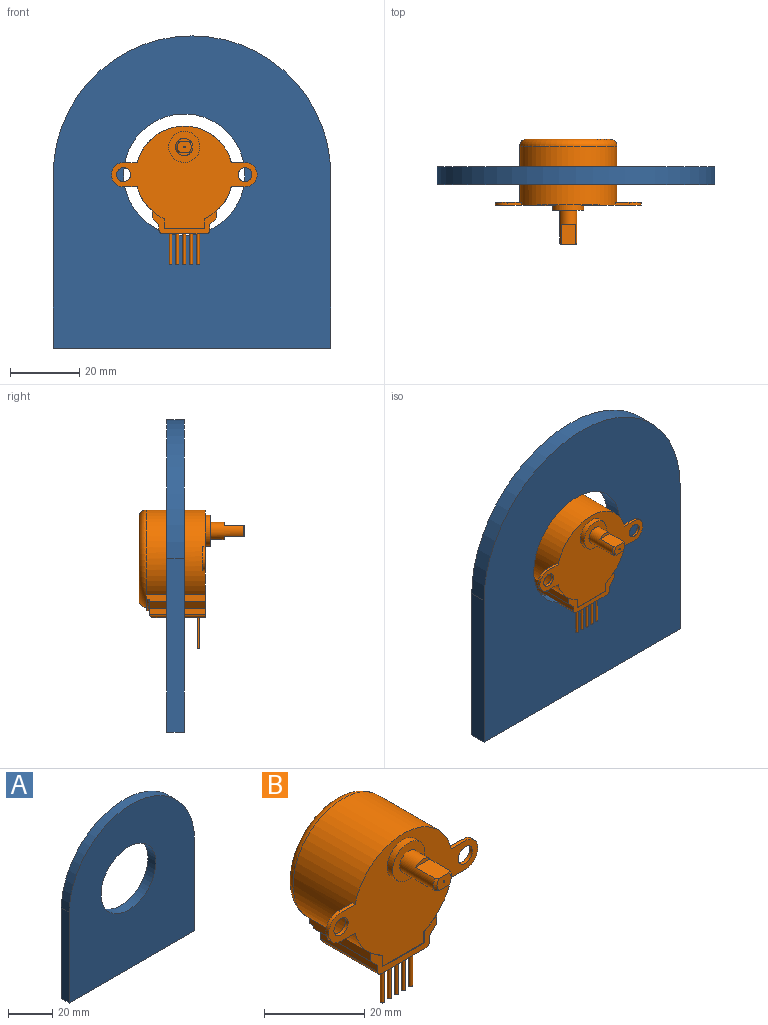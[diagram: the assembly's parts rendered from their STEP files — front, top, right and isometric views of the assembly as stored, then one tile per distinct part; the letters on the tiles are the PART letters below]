
ASSEMBLY  parts=2 mates=1
PART A: 7 faces, bbox 80x5x90 mm
  f0: plane 50x5mm, normal (1,0,0), area 250mm2, adj f1,f4,f5,f6
  f1: cylinder r=40mm len=80mm, axis (0,1,0), area 628.3mm2, adj f0,f2,f5,f6
  f2: plane 50x5mm, normal (-1,0,0), area 250mm2, adj f1,f4,f5,f6
  f3: cylinder r=17.5mm len=35mm, axis (0,1,0), area 549.8mm2, adj f5,f6
  f4: plane 80x5mm, normal (0,0,-1), area 400mm2, adj f0,f2,f5,f6
  f5: plane 90x80mm, normal (0,-1,0), area 5551.2mm2, adj f0,f1,f2,f3,f4
  f6: plane 90x80mm, normal (0,1,0), area 5551.2mm2, adj f0,f1,f2,f3,f4
PART B: 152 faces, bbox 42.1x30.6x41.2 mm
  f0: cone r=500mm half-angle=30deg, axis (0,-1,0), area 0.3mm2, adj f139
  f1: cone r=2.5mm half-angle=45deg, axis (0,1,0), area 2.4mm2, adj f9,f12,f138,f139
  f2: plane 0.8x0.8mm, normal (0,0,-1), area 0.5mm2, adj f66
  f3: plane 24x24mm, normal (0,1,0), area 396.9mm2, adj f15,f16,f21,f22,f23,f24,f25,f26
  f4: cylinder r=14mm len=28mm, axis (0,1,0), area 1138.2mm2, adj f13,f67,f72,f73,f74,f75,f76,f77
  f5: plane 0.88x0.76mm, normal (0,1,0), area 0.5mm2, adj f89
  f6: plane 0.76x0.55mm, normal (0,1,0), area 0.4mm2, adj f107,f109
  f7: plane 0.88x0.59mm, normal (0,1,0), area 0.5mm2, adj f106,f108
  f8: plane 2.91x2.69mm, normal (0,1,0), area 6.3mm2, adj f104,f105,f106,f107,f108,f109,f110
  f9: plane 6.08x4.08mm, normal (0,0,-1), area 23.7mm2, adj f1,f10,f65,f138,f139
  f10: plane 4x1mm, normal (0,-1,0), area 2.8mm2, adj f9,f138
  f11: plane 4x1mm, normal (0,-1,0), area 2.8mm2, adj f12,f138
  f12: plane 6.08x4.08mm, normal (0,0,1), area 23.7mm2, adj f1,f11,f65,f138,f139
  f13: plane 17.16x2.07mm, normal (-1,0,0), area 33.6mm2, adj f4,f14,f54,f56,f60,f61,f62,f64
  f14: torus R=14.8mm, axis (0,1,0), area 6.3mm2, adj f13,f60,f61,f147
  f15: extruded ~2.28x0.58mm, area 0.3mm2, adj f3,f16,f93,f141
  f16: plane 0.86x0.12mm, normal (-0.14,0,-0.99), area 0.1mm2, adj f3,f15,f94,f141
  f17: plane 2.95x2.54mm, normal (0,1,0), area 4.2mm2, adj f18,f19,f20,f21,f22,f23,f24,f25
  f18: plane 0.93x0.78mm, normal (0.76,0,0.65), area 0.1mm2, adj f17,f19,f20,f92
  f19: plane 0.78x0.1mm, normal (0,0,-1), area 0.1mm2, adj f17,f18,f20,f92
  f20: plane 0.93x0.1mm, normal (-1,0,0), area 0.1mm2, adj f17,f18,f19,f92
  f21: plane 0.54x0.1mm, normal (1,0,0), area 0.1mm2, adj f3,f17,f22,f31
  f22: plane 0.36x0.1mm, normal (0,0,1), area 0mm2, adj f3,f17,f21,f23
  f23: plane 0.63x0.1mm, normal (1,0,0), area 0.1mm2, adj f3,f17,f22,f24
  f24: plane 0.36x0.1mm, normal (0,0,-1), area 0mm2, adj f3,f17,f23,f25
  f25: plane 1.79x0.1mm, normal (1,0,0), area 0.2mm2, adj f3,f17,f24,f26
  f26: plane 0.7x0.1mm, normal (0,0,-1), area 0.1mm2, adj f3,f17,f25,f27
  f27: plane 1.75x1.47mm, normal (-0.76,0,-0.64), area 0.2mm2, adj f3,f17,f26,f28
  f28: plane 0.67x0.1mm, normal (-1,0,0), area 0.1mm2, adj f3,f17,f27,f29
  f29: plane 1.47x0.1mm, normal (0,0,1), area 0.1mm2, adj f3,f17,f28,f30
  f30: plane 0.54x0.1mm, normal (-1,0,0), area 0.1mm2, adj f3,f17,f29,f31
  f31: plane 0.7x0.1mm, normal (0,0,1), area 0.1mm2, adj f3,f17,f21,f30
  f32: plane 3x2.38mm, normal (0,1,0), area 5mm2, adj f33,f88,f89,f90
  f33: extruded ~0.67x0.66mm, area 0.2mm2, adj f32,f91
  f34: extruded ~2.42x2mm, area 0.6mm2, adj f3,f35,f86,f140
  f35: plane 0.43x0.1mm, normal (0.99,0,0.15), area 0mm2, adj f3,f34,f36,f140
  f36: plane 1.31x0.1mm, normal (0,0,1), area 0.1mm2, adj f3,f35,f37,f140
  f37: plane 0.64x0.1mm, normal (1,0,0), area 0.1mm2, adj f3,f36,f38,f140
  f38: plane 1.93x0.1mm, normal (0,0,-1), area 0.2mm2, adj f3,f37,f39,f140
  f39: plane 1.56x0.25mm, normal (-0.99,0,-0.16), area 0.2mm2, adj f3,f38,f40,f140
  f40: plane 0.69x0.1mm, normal (-0.14,0,0.99), area 0.1mm2, adj f3,f39,f87,f140
  f41: plane 3.15x2.91mm, normal (0,1,0), area 4.6mm2, adj f42,f43,f44,f45,f46,f47,f48
  f42: plane 2.91x1.08mm, normal (0.94,0,0.35), area 0.3mm2, adj f3,f41,f43,f48
  f43: plane 0.91x0.1mm, normal (0,0,-1), area 0.1mm2, adj f3,f41,f42,f44
  f44: plane 2.09x0.65mm, normal (-0.96,0,-0.3), area 0.2mm2, adj f3,f41,f43,f45
  f45: plane 2.09x0.65mm, normal (0.95,0,-0.3), area 0.2mm2, adj f3,f41,f44,f46
  f46: plane 0.94x0.1mm, normal (0,0,-1), area 0.1mm2, adj f3,f41,f45,f47
  f47: plane 2.91x1.1mm, normal (-0.94,0,0.35), area 0.3mm2, adj f3,f41,f46,f48
  f48: plane 0.97x0.1mm, normal (0,0,1), area 0.1mm2, adj f3,f41,f42,f47
  f49: plane 2.91x2.67mm, normal (0,1,0), area 5.8mm2, adj f50,f51,f83,f84
  f50: plane 1.59x0.1mm, normal (1,0,0), area 0.2mm2, adj f49,f51,f85
  f51: extruded ~1.59x0.87mm, area 0.3mm2, adj f49,f50,f85
  f52: extruded ~1.66x1.15mm, area 0.4mm2, adj f3,f53,f81,f151
  f53: plane 0.79x0.18mm, normal (0.22,0,0.98), area 0.1mm2, adj f3,f52,f82,f151
  f54: plane 18.6x6.54mm, normal (0,-1,0), area 39.8mm2, adj f13,f55,f56,f57,f58,f59,f63,f64
  f55: plane 2.76x0.1mm, normal (1,0,0), area 0.3mm2, adj f54,f56,f59,f67
  f56: cylinder r=14mm len=3.5mm, axis (0,-1,0), area 0.4mm2, adj f13,f54,f55,f67
  f57: cylinder r=14mm len=3.5mm, axis (0,-1,0), area 0.4mm2, adj f54,f58,f67,f147
  f58: plane 2.76x0.1mm, normal (-1,0,0), area 0.3mm2, adj f54,f57,f59,f67
  f59: plane 11.6x0.1mm, normal (0,0,1), area 1.2mm2, adj f54,f55,f58,f67
  f60: plane 18.6x4.34mm, normal (0,1,0), area 16.2mm2, adj f13,f14,f80,f147
  f61: cylinder r=15mm len=18.6mm, axis (0,1,0), area 12mm2, adj f13,f14,f145,f147
  f62: plane 18.6x3.98mm, normal (0,1,0), area 23.6mm2, adj f13,f63,f64,f145,f147,f148,f149,f150
  f63: plane 16.1x1.53mm, normal (-1,0,0), area 24.6mm2, adj f54,f62,f64,f144
  f64: plane 16.1x2mm, normal (-0.71,0,-0.71), area 45.6mm2, adj f13,f54,f62,f63
  f65: cone r=2.5mm half-angle=45deg, axis (0,1,0), area 2.4mm2, adj f9,f12,f138,f139
  f66: cylinder r=0.4mm len=10mm, axis (0,0,-1), area 25.1mm2, adj f2,f137
  f67: plane 42x29.5mm, normal (0,-1,0), area 638.7mm2, adj f4,f55,f56,f57,f58,f59,f68,f70
  f68: cylinder r=4.5mm len=9mm, axis (0,-1,0), area 42.4mm2, adj f67,f69
  f69: plane 9x9mm, normal (0,-1,0), area 44mm2, adj f68,f138
  f70: cylinder r=3.5mm len=7mm, axis (0,1,0), area 8.8mm2, adj f67,f72,f73,f74
  f71: cylinder r=2mm len=4mm, axis (0,1,0), area 10.1mm2, adj f67,f72
  f72: plane 7.44x7mm, normal (0,1,0), area 32.2mm2, adj f4,f70,f71,f73,f74
  f73: plane 3.94x0.8mm, normal (0,0,1), area 3.2mm2, adj f4,f67,f70,f72
  f74: plane 3.94x0.8mm, normal (0,0,-1), area 3.2mm2, adj f4,f67,f70,f72
  f75: plane 7.44x7mm, normal (0,1,0), area 32.2mm2, adj f4,f76,f77,f78,f79
  f76: plane 3.94x0.8mm, normal (0,0,-1), area 3.2mm2, adj f4,f67,f75,f78
  f77: plane 3.94x0.8mm, normal (0,0,1), area 3.2mm2, adj f4,f67,f75,f78
  f78: cylinder r=3.5mm len=7mm, axis (0,1,0), area 8.8mm2, adj f67,f75,f76,f77
  f79: cylinder r=2mm len=4mm, axis (0,1,0), area 10.1mm2, adj f67,f75
  f80: torus R=12mm, axis (0,1,0), area 262mm2, adj f3,f4,f60
  f81: plane 0.78x0.24mm, normal (0.29,0,-0.96), area 0.1mm2, adj f3,f52,f82,f151
  f82: extruded ~3x2.83mm, area 0.8mm2, adj f3,f53,f81,f151
  f83: extruded ~2.91x2.67mm, area 0.7mm2, adj f3,f49,f84
  f84: plane 2.91x0.1mm, normal (-1,0,0), area 0.3mm2, adj f3,f49,f83
  f85: plane 1.59x0.87mm, normal (0,1,0), area 1.3mm2, adj f50,f51
  f86: plane 0.82x0.1mm, normal (-0.11,0,-0.99), area 0.1mm2, adj f3,f34,f87,f140
  f87: extruded ~1.02x0.82mm, area 0.3mm2, adj f3,f40,f86,f140
  f88: extruded ~2.19x1.39mm, area 0.5mm2, adj f3,f32,f90
  f89: extruded ~0.87x0.76mm, area 0.3mm2, adj f5,f32
  f90: extruded ~2.38x1.61mm, area 0.5mm2, adj f3,f32,f88
  f91: plane 0.67x0.66mm, normal (0,1,0), area 0.4mm2, adj f33
  f92: plane 0.93x0.78mm, normal (0,1,0), area 0.4mm2, adj f18,f19,f20
  f93: plane 0.9x0.1mm, normal (0,0,-1), area 0.1mm2, adj f3,f15,f94,f141
  f94: extruded ~2.95x2.34mm, area 0.5mm2, adj f3,f16,f93,f141
  f95: plane 1.22x0.1mm, normal (-1,0,0), area 0.1mm2, adj f3,f96,f103,f142
  f96: plane 1.69x1.13mm, normal (-0.83,0,0.56), area 0.2mm2, adj f3,f95,f97,f142
  f97: plane 1x0.1mm, normal (0,0,-1), area 0.1mm2, adj f3,f96,f98,f142
  f98: plane 0.97x0.59mm, normal (0.86,0,-0.52), area 0.1mm2, adj f3,f97,f99,f142
  f99: plane 0.97x0.59mm, normal (-0.86,0,-0.52), area 0.1mm2, adj f3,f98,f100,f142
  f100: plane 0.99x0.1mm, normal (0,0,-1), area 0.1mm2, adj f3,f99,f101,f142
  f101: plane 1.69x1.13mm, normal (0.83,0,0.56), area 0.2mm2, adj f3,f100,f102,f142
  f102: plane 1.22x0.1mm, normal (1,0,0), area 0.1mm2, adj f3,f101,f103,f142
  f103: plane 0.9x0.1mm, normal (0,0,1), area 0.1mm2, adj f3,f95,f102,f142
  f104: extruded ~2.69x1.55mm, area 0.4mm2, adj f3,f8,f105,f110
  f105: plane 2.91x0.1mm, normal (-1,0,0), area 0.3mm2, adj f3,f8,f104,f110
  f106: plane 0.59x0.1mm, normal (1,0,0), area 0.1mm2, adj f7,f8,f108
  f107: plane 0.55x0.1mm, normal (1,0,0), area 0.1mm2, adj f6,f8,f109
  f108: extruded ~0.88x0.59mm, area 0.2mm2, adj f7,f8,f106
  f109: extruded ~0.76x0.55mm, area 0.2mm2, adj f6,f8,f107
  f110: extruded ~2.55x1.36mm, area 0.4mm2, adj f3,f8,f104,f105
  f111: extruded ~2.19x1.39mm, area 0.5mm2, adj f3,f114,f143
  f112: extruded ~0.87x0.76mm, area 0.3mm2, adj f116,f143
  f113: extruded ~0.67x0.66mm, area 0.2mm2, adj f115,f143
  f114: extruded ~2.38x1.61mm, area 0.5mm2, adj f3,f111,f143
  f115: plane 0.67x0.66mm, normal (0,1,0), area 0.4mm2, adj f113
  f116: plane 0.88x0.76mm, normal (0,1,0), area 0.5mm2, adj f112
  f117: plane 1.26x0.1mm, normal (0,0,-1), area 0.1mm2, adj f3,f118,f122,f123
  f118: plane 0.66x0.1mm, normal (1,0,0), area 0.1mm2, adj f3,f117,f119,f123
  f119: plane 2.42x0.1mm, normal (0,0,1), area 0.2mm2, adj f3,f118,f120,f123
  f120: extruded ~2.4x1.6mm, area 0.4mm2, adj f3,f119,f121,f123
  f121: plane 0.81x0.1mm, normal (-0.08,0,1), area 0.1mm2, adj f3,f120,f122,f123
  f122: extruded ~2.34x2.3mm, area 0.5mm2, adj f3,f117,f121,f123
  f123: plane 2.95x2.42mm, normal (0,1,0), area 4.5mm2, adj f117,f118,f119,f120,f121,f122
  f124: plane 15.1x12.6mm, normal (0,0,-1), area 181.5mm2, adj f54,f125,f126,f127,f128,f144,f146,f148
  f125: plane 8x1mm, normal (0,1,0), area 8mm2, adj f124,f126,f128,f137
  f126: cylinder r=0.5mm len=1mm, axis (0,0,-1), area 1.6mm2, adj f124,f125,f127,f137
  f127: plane 8x1mm, normal (0,-1,0), area 8mm2, adj f124,f126,f128,f137
  f128: cylinder r=0.5mm len=1mm, axis (0,0,-1), area 1.6mm2, adj f124,f125,f127,f137
  f129: cylinder r=0.4mm len=10mm, axis (0,0,-1), area 25.1mm2, adj f130,f137
  f130: plane 0.8x0.8mm, normal (0,0,-1), area 0.5mm2, adj f129
  f131: cylinder r=0.4mm len=10mm, axis (0,0,-1), area 25.1mm2, adj f132,f137
  f132: plane 0.8x0.8mm, normal (0,0,-1), area 0.5mm2, adj f131
  f133: cylinder r=0.4mm len=10mm, axis (0,0,-1), area 25.1mm2, adj f134,f137
  f134: plane 0.8x0.8mm, normal (0,0,-1), area 0.5mm2, adj f133
  f135: cylinder r=0.4mm len=10mm, axis (0,0,-1), area 25.1mm2, adj f136,f137
  f136: plane 0.8x0.8mm, normal (0,0,-1), area 0.5mm2, adj f135
  f137: plane 9x1mm, normal (0,0,-1), area 6.3mm2, adj f66,f125,f126,f127,f128,f129,f131,f133
  f138: cylinder r=2.5mm len=9.5mm, axis (0,-1,0), area 98.2mm2, adj f1,f9,f10,f11,f12,f65,f69
  f139: plane 4x3mm, normal (0,-1,0), area 10.6mm2, adj f0,f1,f9,f12,f65
  f140: plane 2.95x2.42mm, normal (0,1,0), area 4.5mm2, adj f34,f35,f36,f37,f38,f39,f40,f86
  f141: plane 2.95x2.34mm, normal (0,1,0), area 3.6mm2, adj f15,f16,f93,f94
  f142: plane 3.16x2.91mm, normal (0,1,0), area 4mm2, adj f95,f96,f97,f98,f99,f100,f101,f102
  f143: plane 3x2.38mm, normal (0,1,0), area 5mm2, adj f111,f112,f113,f114
  f144: cylinder r=1mm len=16.1mm, axis (0,1,0), area 24.5mm2, adj f54,f63,f124,f148
  f145: torus R=15.2mm, axis (0,1,0), area 6.3mm2, adj f13,f61,f62,f147
  f146: cylinder r=1mm len=16.1mm, axis (0,1,0), area 24.5mm2, adj f54,f124,f148,f149
  f147: plane 17.16x2.07mm, normal (1,0,0), area 33.6mm2, adj f4,f14,f54,f57,f60,f61,f62,f145
  f148: cylinder r=1mm len=14.6mm, axis (-1,0,0), area 21.4mm2, adj f62,f124,f144,f146
  f149: plane 16.1x1.53mm, normal (1,0,0), area 24.6mm2, adj f54,f62,f146,f150
  f150: plane 16.1x2mm, normal (0.71,0,-0.71), area 45.6mm2, adj f54,f62,f147,f149
  f151: plane 3x2.83mm, normal (0,1,0), area 4.8mm2, adj f52,f53,f81,f82
PLACE A t=(-1.47,6.94,6.8)mm
PLACE B t=(-1.47,-4.06,6.8)mm
MATE revolute A.f3 <-> B.f4  axis (0,1,0) through (-1.47,4.44,6.8)mm
